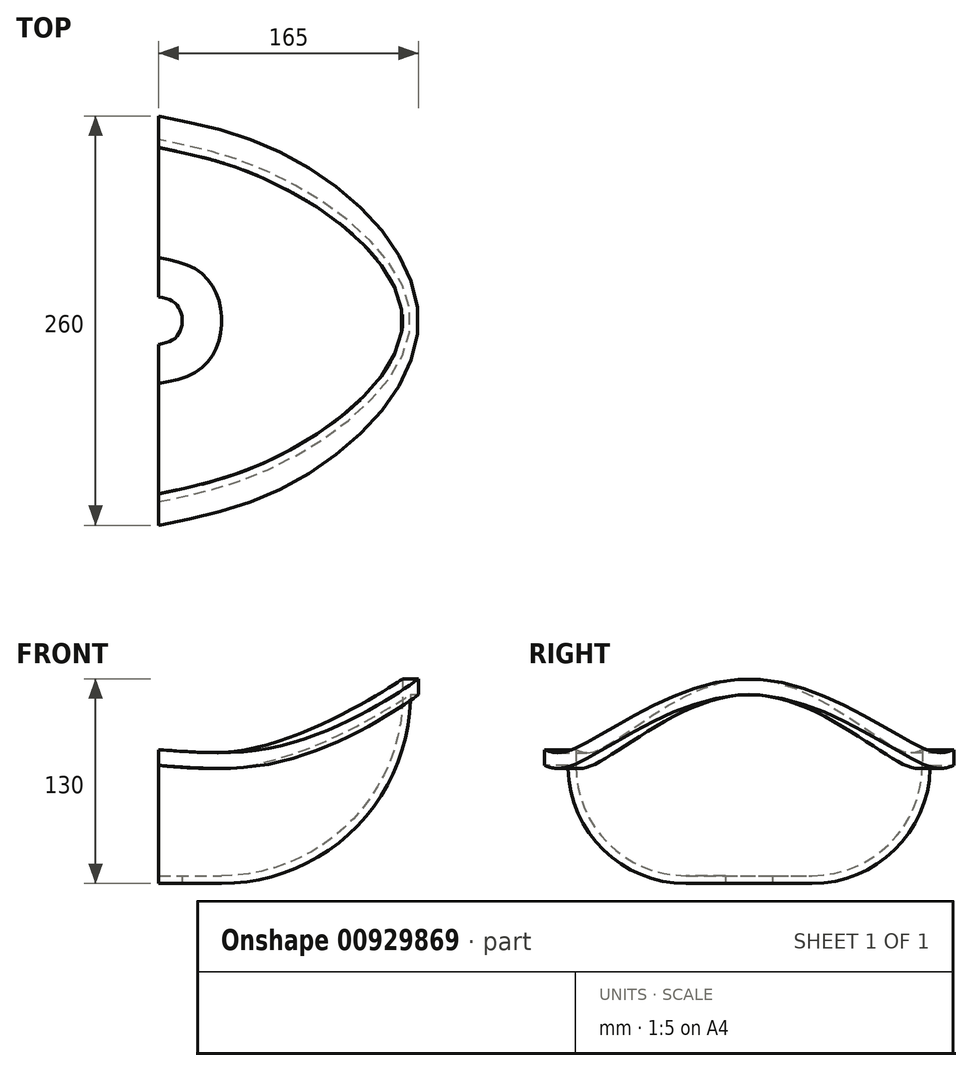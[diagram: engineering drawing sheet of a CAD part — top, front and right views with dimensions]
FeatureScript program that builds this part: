
annotation { "Feature Type Name" : "Feature", "Feature Type Description" : "" }
export const myFeature = defineFeature(function(context is Context, id is Id, definition is map)
    precondition{}
    {
        {
            var Q0;
            Q0=qCreatedBy(makeId("Front.planeOp"),FACE);
            var sketch = newSketch(context, id + "F0", { "sketchPlane" : qUnion([Q0])});
            skArc(sketch, "E0", {"start": v(40, 0) * mm, "mid": v(124.85, 35.15) * mm, "end": v(160, 120) * mm});
            skArc(sketch, "E1", {"start": v(40, 5) * mm, "mid": v(121.32, 38.68) * mm, "end": v(155, 120) * mm});
            skLineSegment(sketch, "E2.bottom", {"start": v(15, 5) * mm, "end": v(40, 5) * mm});
            skLineSegment(sketch, "E2.top", {"start": v(15, 0) * mm, "end": v(40, 0) * mm});
            skLineSegment(sketch, "E2.left", {"start": v(15, 5) * mm, "end": v(15, 0) * mm});
            skLineSegment(sketch, "E2.right", {"start": v(40, 5) * mm, "end": v(40, 0) * mm, "construction": true});
            skLineSegment(sketch, "E3.bottom", {"start": v(155, 130) * mm, "end": v(165, 130) * mm});
            skLineSegment(sketch, "E3.top", {"start": v(160, 120) * mm, "end": v(165, 120) * mm});
            skLineSegment(sketch, "E3.left", {"start": v(155, 130) * mm, "end": v(155, 120) * mm});
            skLineSegment(sketch, "E3.right", {"start": v(165, 130) * mm, "end": v(165, 120) * mm});
            skLineSegment(sketch, "E4", {"start": v(0, 0) * mm, "end": v(0, 50) * mm, "construction": true});
            skSolve(sketch);
        }
        {
            var Q0;
            Q0=sQuery(id+"F0.wireOp",EDGE,"E4");
            cPlane(context, id + "F1", {"entities" : qUnion([Q0]), "cplaneType" : CPlaneType.LINE_ANGLE, "offset" : 25.4 * mm, "angle" : 30 * degree, "oppositeDirection" : true, "width" : 152.4 * mm, "height" : 152.4 * mm});
        }
        {
            var Q0;
            Q0=qCreatedBy(id+"F1.planeOp",FACE);
            var sketch = newSketch(context, id + "F2", { "sketchPlane" : qUnion([Q0])});
            skArc(sketch, "E5", {"start": v(40, 0) * mm, "mid": v(93.03, 21.97) * mm, "end": v(115, 75) * mm});
            skArc(sketch, "E6", {"start": v(40, 5) * mm, "mid": v(89.5, 25.5) * mm, "end": v(110, 75) * mm});
            skLineSegment(sketch, "E7.bottom", {"start": v(15, 5) * mm, "end": v(40, 5) * mm});
            skLineSegment(sketch, "E7.top", {"start": v(15, 0) * mm, "end": v(40, 0) * mm});
            skLineSegment(sketch, "E7.left", {"start": v(15, 5) * mm, "end": v(15, 0) * mm});
            skLineSegment(sketch, "E7.right", {"start": v(40, 5) * mm, "end": v(40, 0) * mm, "construction": true});
            skLineSegment(sketch, "E8.bottom", {"start": v(110, 85) * mm, "end": v(130, 85) * mm});
            skLineSegment(sketch, "E8.top", {"start": v(115, 75) * mm, "end": v(130, 75) * mm});
            skLineSegment(sketch, "E8.left", {"start": v(110, 85) * mm, "end": v(110, 75) * mm});
            skLineSegment(sketch, "E8.right", {"start": v(130, 85) * mm, "end": v(130, 75) * mm});
            skLineSegment(sketch, "E9", {"start": v(0, 0) * mm, "end": v(0, 50) * mm, "construction": true});
            skSolve(sketch);
        }
        {
            var Q0;
            Q0=sQuery(id+"F2.wireOp",EDGE,"E9");
            cPlane(context, id + "F3", {"entities" : qUnion([Q0]), "cplaneType" : CPlaneType.LINE_ANGLE, "offset" : 25.4 * mm, "angle" : 150 * degree, "oppositeDirection" : true, "width" : 152.4 * mm, "height" : 152.4 * mm});
        }
        {
            var Q0;
            Q0=qCreatedBy(id+"F3.planeOp",FACE);
            var sketch = newSketch(context, id + "F4", { "sketchPlane" : qUnion([Q0])});
            skArc(sketch, "E10", {"start": v(40, 0) * mm, "mid": v(93.03, 21.97) * mm, "end": v(115, 75) * mm});
            skArc(sketch, "E11", {"start": v(40, 5) * mm, "mid": v(89.5, 25.5) * mm, "end": v(110, 75) * mm});
            skLineSegment(sketch, "E12.bottom", {"start": v(15, 5) * mm, "end": v(40, 5) * mm});
            skLineSegment(sketch, "E12.top", {"start": v(15, 0) * mm, "end": v(40, 0) * mm});
            skLineSegment(sketch, "E12.left", {"start": v(15, 5) * mm, "end": v(15, 0) * mm});
            skLineSegment(sketch, "E12.right", {"start": v(40, 5) * mm, "end": v(40, 0) * mm, "construction": true});
            skLineSegment(sketch, "E13.bottom", {"start": v(110, 85) * mm, "end": v(130, 85) * mm});
            skLineSegment(sketch, "E13.top", {"start": v(115, 75) * mm, "end": v(130, 75) * mm});
            skLineSegment(sketch, "E13.left", {"start": v(110, 85) * mm, "end": v(110, 75) * mm});
            skLineSegment(sketch, "E13.right", {"start": v(130, 85) * mm, "end": v(130, 75) * mm});
            skLineSegment(sketch, "E14", {"start": v(0, 0) * mm, "end": v(0, 50) * mm, "construction": true});
            skSolve(sketch);
        }
        {
            var Q0;
            Q0=qCreatedBy(makeId("Right.planeOp"),FACE);
            var sketch = newSketch(context, id + "F5", { "sketchPlane" : qUnion([Q0])});
            skArc(sketch, "E15", {"start": v(40, 0) * mm, "mid": v(93.03, 21.97) * mm, "end": v(115, 75) * mm});
            skArc(sketch, "E16", {"start": v(40, 5) * mm, "mid": v(89.5, 25.5) * mm, "end": v(110, 75) * mm});
            skLineSegment(sketch, "E17.bottom", {"start": v(15, 5) * mm, "end": v(40, 5) * mm});
            skLineSegment(sketch, "E17.top", {"start": v(15, 0) * mm, "end": v(40, 0) * mm});
            skLineSegment(sketch, "E17.left", {"start": v(15, 5) * mm, "end": v(15, 0) * mm});
            skLineSegment(sketch, "E17.right", {"start": v(40, 5) * mm, "end": v(40, 0) * mm, "construction": true});
            skLineSegment(sketch, "E18.bottom", {"start": v(110, 85) * mm, "end": v(130, 85) * mm});
            skLineSegment(sketch, "E18.top", {"start": v(115, 75) * mm, "end": v(130, 75) * mm});
            skLineSegment(sketch, "E18.left", {"start": v(110, 85) * mm, "end": v(110, 75) * mm});
            skLineSegment(sketch, "E18.right", {"start": v(130, 85) * mm, "end": v(130, 75) * mm});
            skLineSegment(sketch, "E19", {"start": v(0, 0) * mm, "end": v(0, 50) * mm, "construction": true});
            skSolve(sketch);
        }
        {
            var Q0;
            Q0=sQuery(id+"F5.wireOp",EDGE,"E19");
            cPlane(context, id + "F6", {"entities" : qUnion([Q0]), "cplaneType" : CPlaneType.LINE_ANGLE, "offset" : 25.4 * mm, "angle" : 180 * degree, "width" : 152.4 * mm, "height" : 152.4 * mm});
        }
        {
            var Q0;
            Q0=qCreatedBy(id+"F6.planeOp",FACE);
            var sketch = newSketch(context, id + "F7", { "sketchPlane" : qUnion([Q0])});
            skArc(sketch, "E20", {"start": v(40, 0) * mm, "mid": v(93.03, 21.97) * mm, "end": v(115, 75) * mm});
            skArc(sketch, "E21", {"start": v(40, 5) * mm, "mid": v(89.5, 25.5) * mm, "end": v(110, 75) * mm});
            skLineSegment(sketch, "E22.bottom", {"start": v(15, 5) * mm, "end": v(40, 5) * mm});
            skLineSegment(sketch, "E22.top", {"start": v(15, 0) * mm, "end": v(40, 0) * mm});
            skLineSegment(sketch, "E22.left", {"start": v(15, 5) * mm, "end": v(15, 0) * mm});
            skLineSegment(sketch, "E22.right", {"start": v(40, 5) * mm, "end": v(40, 0) * mm, "construction": true});
            skLineSegment(sketch, "E23.bottom", {"start": v(110, 85) * mm, "end": v(130, 85) * mm});
            skLineSegment(sketch, "E23.top", {"start": v(115, 75) * mm, "end": v(130, 75) * mm});
            skLineSegment(sketch, "E23.left", {"start": v(110, 85) * mm, "end": v(110, 75) * mm});
            skLineSegment(sketch, "E23.right", {"start": v(130, 85) * mm, "end": v(130, 75) * mm});
            skLineSegment(sketch, "E24", {"start": v(0, 0) * mm, "end": v(0, 50) * mm, "construction": true});
            skSolve(sketch);
        }
        {
            var Q0;
            Q0=makeQuery(id+"F7.imprint","IMPRINT",FACE,{"disambiguationData":[TD([[makeQuery(id+"F7.imprint","IMPRINT",EDGE,{"derivedFrom":sQuery(id+"F7.wireOp",EDGE,"E20")}),1.0]])]});
            var Q1;
            Q1=makeQuery(id+"F4.imprint","IMPRINT",FACE,{"disambiguationData":[TD([[makeQuery(id+"F4.imprint","IMPRINT",EDGE,{"derivedFrom":sQuery(id+"F4.wireOp",EDGE,"E10")}),1.0]])]});
            var Q2;
            Q2=makeQuery(id+"F0.imprint","IMPRINT",FACE,{"disambiguationData":[TD([[makeQuery(id+"F0.imprint","IMPRINT",EDGE,{"derivedFrom":sQuery(id+"F0.wireOp",EDGE,"E0")}),1.0]])]});
            var Q3;
            Q3=makeQuery(id+"F2.imprint","IMPRINT",FACE,{"disambiguationData":[TD([[makeQuery(id+"F2.imprint","IMPRINT",EDGE,{"derivedFrom":sQuery(id+"F2.wireOp",EDGE,"E5")}),1.0]])]});
            var Q4;
            Q4=makeQuery(id+"F5.imprint","IMPRINT",FACE,{"disambiguationData":[TD([[makeQuery(id+"F5.imprint","IMPRINT",EDGE,{"derivedFrom":sQuery(id+"F5.wireOp",EDGE,"E15")}),1.0]])]});
            loft(context, id + "F8", {"sheetProfilesArray" : [{ "sheetProfileEntities" : qUnion([Q0]) }, { "sheetProfileEntities" : qUnion([Q1]) }, { "sheetProfileEntities" : qUnion([Q2]) }, { "sheetProfileEntities" : qUnion([Q3]) }, { "sheetProfileEntities" : qUnion([Q4]) }]});
        }
    });
